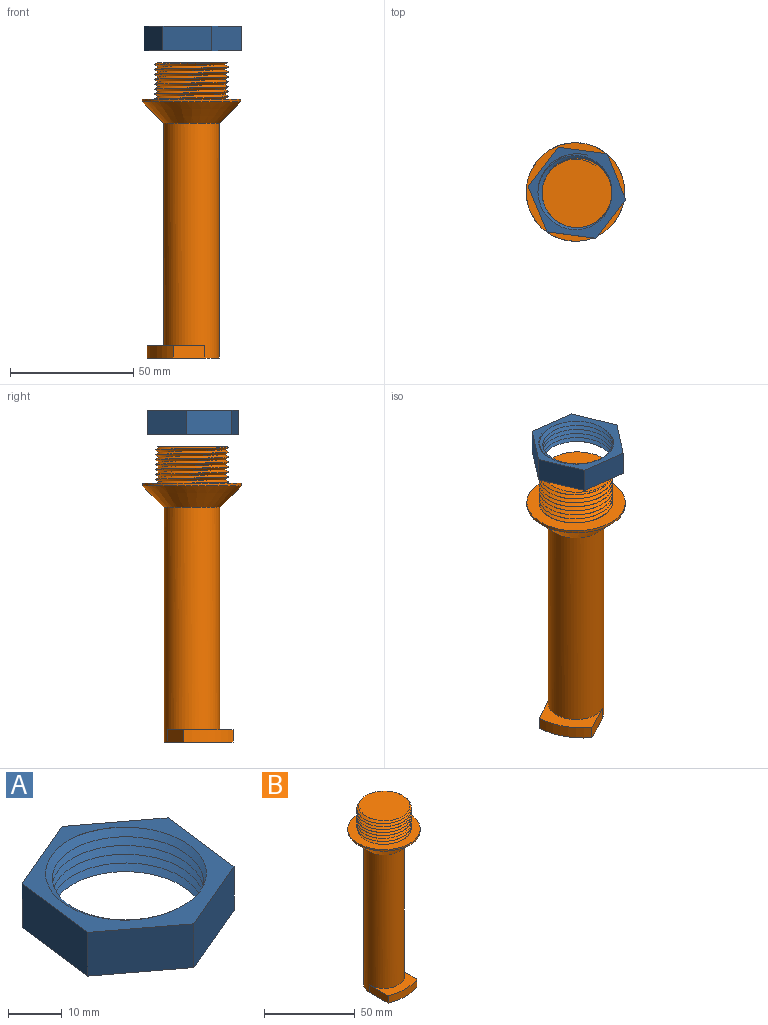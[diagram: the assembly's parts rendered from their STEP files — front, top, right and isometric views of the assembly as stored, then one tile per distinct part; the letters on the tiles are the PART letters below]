
ASSEMBLY  parts=2 mates=1
PART A: 11 faces, bbox 38.4x41.3x13.9 mm
  f0: bspline ~36.59x31.69mm, area 919.3mm2, adj f1,f7,f9,f10
  f1: bspline ~36.59x31.69mm, area 918.4mm2, adj f0,f7,f9,f10
  f2: plane 18.41x10mm, normal (-0.39,0.92,0), area 200mm2, adj f3,f8,f9,f10
  f3: plane 19.85x10mm, normal (-0.99,0.12,0), area 200mm2, adj f2,f4,f9,f10
  f4: plane 15.98x12.03mm, normal (-0.6,-0.8,0), area 200mm2, adj f3,f5,f9,f10
  f5: plane 18.41x10mm, normal (0.39,-0.92,0), area 200mm2, adj f4,f6,f9,f10
  f6: plane 19.85x10mm, normal (0.99,-0.12,0), area 200mm2, adj f5,f8,f9,f10
  f7: cylinder r=15.85mm len=31.69mm, axis (0,0,-1), area 26.7mm2, adj f0,f1,f9,f10
  f8: plane 15.98x12.03mm, normal (0.6,0.8,0), area 200mm2, adj f2,f6,f9,f10
  f9: plane 41.22x38.33mm, normal (0,0,-1), area 329.5mm2, adj f0,f1,f2,f3,f4,f5,f6,f7
  f10: plane 41.25x38.36mm, normal (0,0,1), area 329.5mm2, adj f0,f1,f2,f3,f4,f5,f6,f7
PART B: 13 faces, bbox 41.4x41.4x122.7 mm
  f0: cylinder r=15mm len=30mm, axis (0,0,-1), area 87.3mm2, adj f1,f2,f3,f12
  f1: bspline ~34.64x30mm, area 1307.5mm2, adj f0,f2,f3,f12
  f2: bspline ~34.64x30mm, area 1306.1mm2, adj f0,f1,f3,f12
  f3: plane 41.44x41.44mm, normal (0,0,1), area 624.4mm2, adj f0,f1,f2,f4
  f4: cylinder r=20mm len=40mm, axis (0,0,1), area 125.7mm2, adj f3,f11
  f5: cylinder r=11.25mm len=95.25mm, axis (0,0,1), area 6556.1mm2, adj f6,f7,f9,f10,f11
  f6: plane 22.5x16.75mm, normal (0,0,1), area 160.7mm2, adj f5,f7,f8,f9
  f7: plane 14.39x5mm, normal (1,0,0), area 72mm2, adj f5,f6,f8,f10
  f8: cylinder r=28mm len=22.5mm, axis (0,0,1), area 115.8mm2, adj f6,f7,f9,f10
  f9: plane 14.39x5mm, normal (-1,0,0), area 72mm2, adj f5,f6,f8,f10
  f10: plane 28x22.5mm, normal (0,0,-1), area 558.3mm2, adj f5,f7,f8,f9
  f11: cone r=11mm half-angle=45deg, axis (0,0,1), area 1214.9mm2, adj f4,f5
  f12: plane 29.82x29.82mm, normal (0,0,1), area 632.2mm2, adj f0,f1,f2
PLACE A rot(axis=(0,0,1),89.5deg) t=(45.29,46.5,-34.65)mm
PLACE B rot(axis=(0,0,-1),62.2deg) t=(44.7,46.86,-64.5)mm fixed
MATE cylindrical A.f7 <-> B.f12  axis (0,0,1) through (45.29,46.5,-34.65)mm
